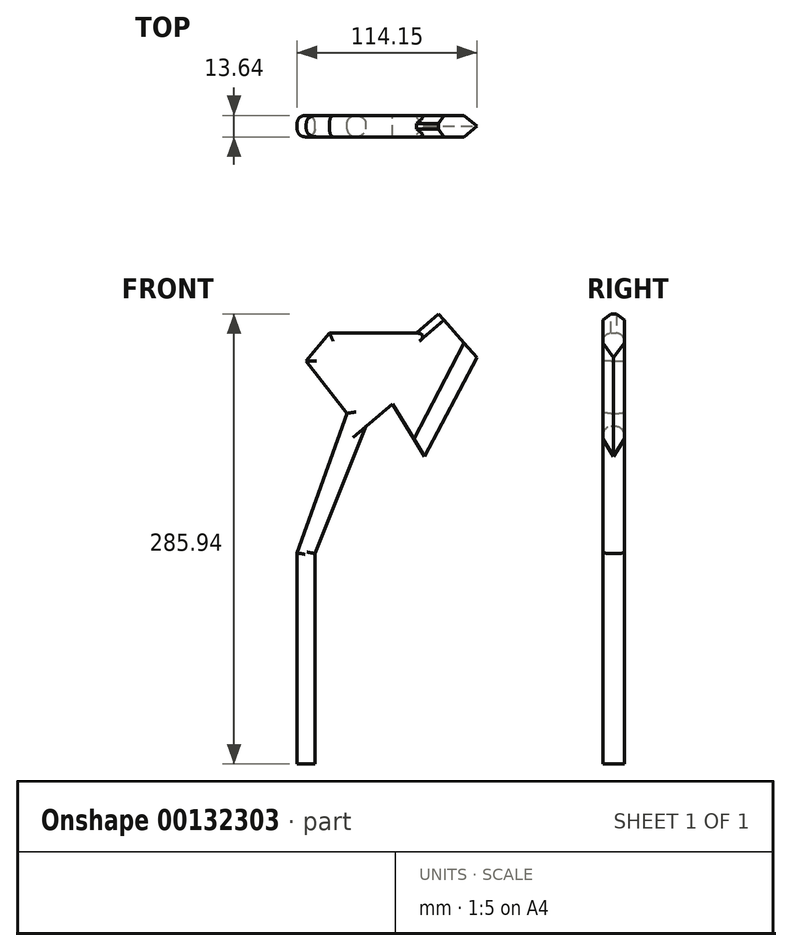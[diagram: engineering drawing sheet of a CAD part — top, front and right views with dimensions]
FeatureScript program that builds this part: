
annotation { "Feature Type Name" : "Feature", "Feature Type Description" : "" }
export const myFeature = defineFeature(function(context is Context, id is Id, definition is map)
    precondition{}
    {
        {
            var Q0;
            Q0=qCreatedBy(makeId("Front.planeOp"),FACE);
            var sketch = newSketch(context, id + "F0", { "sketchPlane" : qUnion([Q0])});
            skLineSegment(sketch, "E0", {"start": v(16.84, 14.27) * mm, "end": v(38, -20.68) * mm});
            skLineSegment(sketch, "E1", {"start": v(38, -20.68) * mm, "end": v(71.3, 42.47) * mm});
            skLineSegment(sketch, "E2", {"start": v(71.3, 42.47) * mm, "end": v(46, 71.3) * mm});
            skLineSegment(sketch, "E3", {"start": v(46, 71.3) * mm, "end": v(32.13, 59.14) * mm});
            skLineSegment(sketch, "E4", {"start": v(32.13, 59.14) * mm, "end": v(-23.25, 59.14) * mm});
            skLineSegment(sketch, "E5", {"start": v(-23.25, 59.14) * mm, "end": v(-38, 41.53) * mm});
            skLineSegment(sketch, "E6", {"start": v(-38, 41.53) * mm, "end": v(-12.03, 8.18) * mm});
            skLineSegment(sketch, "E7", {"start": v(-12.03, 8.18) * mm, "end": v(-43.79, -80.49) * mm});
            skLineSegment(sketch, "E8", {"start": v(-43.79, -80.49) * mm, "end": v(-43.79, -214.64) * mm});
            skLineSegment(sketch, "E9", {"start": v(-43.79, -214.64) * mm, "end": v(-32.46, -214.64) * mm});
            skLineSegment(sketch, "E10", {"start": v(-32.46, -214.64) * mm, "end": v(-32.46, -80.89) * mm});
            skLineSegment(sketch, "E11", {"start": v(-32.46, -80.89) * mm, "end": v(0, 0) * mm});
            skLineSegment(sketch, "E12", {"start": v(0, 0) * mm, "end": v(16.84, 14.27) * mm});
            skLineSegment(sketch, "E13", {"start": v(-43.79, -80.49) * mm, "end": v(-32.46, -80.89) * mm});
            skSolve(sketch);
        }
        {
            var Q0;
            Q0 = qSketchRegion(id + "F0", true);
            extrude(context, id + "F1", {"entities" : qUnion([Q0]), "depth" : 13.64 * mm});
        }
        {
            var Q0;
            Q0=makeQuery(id+"F1.opExtrude","CAP_EDGE",EDGE,{"disambiguationData":[OSD([sQuery(id+"F0.wireOp",EDGE,"E1")])],"isStart":false});
            var Q1;
            Q1=makeQuery(id+"F1.opExtrude","CAP_EDGE",EDGE,{"disambiguationData":[OSD([sQuery(id+"F0.wireOp",EDGE,"E1")])],"isStart":true});
            chamfer(context, id + "F2", {"entities" : qUnion([Q0, Q1]), "chamferType" : ChamferType.TWO_OFFSETS, "width1" : 7.62 * mm, "oppositeDirection" : true, "width2" : 12.7 * mm, "tangentPropagation" : true});
        }
        {
            var Q0;
            Q0=makeQuery(id+"F1.opExtrude","CAP_EDGE",EDGE,{"disambiguationData":[OSD([sQuery(id+"F0.wireOp",EDGE,"E10")])],"isStart":false});
            var Q1;
            Q1=makeQuery(id+"F1.opExtrude","CAP_EDGE",EDGE,{"disambiguationData":[OSD([sQuery(id+"F0.wireOp",EDGE,"E10")])],"isStart":true});
            var Q2;
            Q2=makeQuery(id+"F1.opExtrude","CAP_EDGE",EDGE,{"disambiguationData":[OSD([sQuery(id+"F0.wireOp",EDGE,"E8")])],"isStart":false});
            var Q3;
            Q3=makeQuery(id+"F1.opExtrude","CAP_EDGE",EDGE,{"disambiguationData":[OSD([sQuery(id+"F0.wireOp",EDGE,"E8")])],"isStart":true});
            var Q4;
            Q4=makeQuery(id+"F1.opExtrude","CAP_EDGE",EDGE,{"disambiguationData":[OSD([sQuery(id+"F0.wireOp",EDGE,"E11")])],"isStart":false});
            var Q5;
            Q5=makeQuery(id+"F1.opExtrude","CAP_EDGE",EDGE,{"disambiguationData":[OSD([sQuery(id+"F0.wireOp",EDGE,"E7")])],"isStart":false});
            var Q6;
            Q6=makeQuery(id+"F1.opExtrude","CAP_EDGE",EDGE,{"disambiguationData":[OSD([sQuery(id+"F0.wireOp",EDGE,"E7")])],"isStart":true});
            var Q7;
            Q7=makeQuery(id+"F1.opExtrude","CAP_EDGE",EDGE,{"disambiguationData":[OSD([sQuery(id+"F0.wireOp",EDGE,"E11")])],"isStart":true});
            fillet(context, id + "F3", {"entities" : qUnion([Q0, Q1, Q2, Q3, Q4, Q5, Q6, Q7]), "radius" : 5.08 * mm, "tangentPropagation" : true, "allowEdgeOverflow" : false});
        }
        {
            var Q0;
            Q0=makeQuery(id+"F1.opExtrude","CAP_EDGE",EDGE,{"disambiguationData":[OSD([sQuery(id+"F0.wireOp",EDGE,"E3")])],"isStart":false});
            var Q1;
            Q1=makeQuery(id+"F1.opExtrude","CAP_EDGE",EDGE,{"disambiguationData":[OSD([sQuery(id+"F0.wireOp",EDGE,"E3")])],"isStart":true});
            chamfer(context, id + "F4", {"entities" : qUnion([Q0, Q1]), "width" : 5.08 * mm, "tangentPropagation" : true});
        }
        {
            var Q0;
            Q0=makeQuery(id+"F1.opExtrude","CAP_EDGE",EDGE,{"disambiguationData":[OSD([sQuery(id+"F0.wireOp",EDGE,"E5")])],"isStart":false});
            var Q1;
            Q1=makeQuery(id+"F1.opExtrude","CAP_EDGE",EDGE,{"disambiguationData":[OSD([sQuery(id+"F0.wireOp",EDGE,"E5")])],"isStart":true});
            var Q2;
            Q2=makeQuery(id+"F1.opExtrude","CAP_EDGE",EDGE,{"disambiguationData":[OSD([sQuery(id+"F0.wireOp",EDGE,"E6")])],"isStart":true});
            var Q3;
            Q3=makeQuery(id+"F1.opExtrude","CAP_EDGE",EDGE,{"disambiguationData":[OSD([sQuery(id+"F0.wireOp",EDGE,"E6")])],"isStart":false});
            var Q4;
            Q4=makeQuery(id+"F1.opExtrude","CAP_EDGE",EDGE,{"disambiguationData":[OSD([sQuery(id+"F0.wireOp",EDGE,"E4")])],"isStart":false});
            var Q5;
            Q5=makeQuery(id+"F1.opExtrude","CAP_EDGE",EDGE,{"disambiguationData":[OSD([sQuery(id+"F0.wireOp",EDGE,"E4")])],"isStart":true});
            fillet(context, id + "F5", {"entities" : qUnion([Q0, Q1, Q2, Q3, Q4, Q5]), "radius" : 5.08 * mm, "tangentPropagation" : true, "allowEdgeOverflow" : false});
        }
    });
